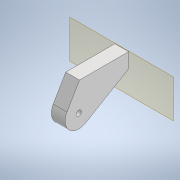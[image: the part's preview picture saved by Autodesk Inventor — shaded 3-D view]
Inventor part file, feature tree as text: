
AUTODESK INVENTOR PART (.ipt)
format: ipt  version: 2022 (Build 260153000, 153)  size: 130,048 bytes
history: native  units: in
note: dims shown in document units (in); Inventor stores cm internally (conversion verified against a paired STEP export)
features: reference x5, other x3, extrude x2, sketch x2, plane x1
ambient origin geometry x8: Origin, YZ Plane, XZ Plane, XY Plane, X Axis, Y Axis, Z Axis, Center Point
bodies: Solid1 (feature_tree)
feature tree (13):
  plane  "Work Plane1"
  extrude  "Extrusion1"  Depth=0.0079in
  extrude  "Extrusion2"  Depth=0.4724in
  sketch  "Sketch1"  dims[d0=0.0079in d1=0.0079in]
  reference  "Reference1"
  reference  "Reference4"
  reference  "Reference5"
  reference  "Reference6"
  sketch  "Sketch2"  dims[d3=0.1575in d4=0.1575in d5=1.5748in d6=0.0in d7=0.1693in d8=1.5748in d9=0.0in d10=0.1575in d11=0.1181in d12=0.1181in d14=0.4724in]
  reference  "Reference7"
  other  "Linear Rail Assembly.iam"
  other  "pivot module base:1"
  other  "cantilever:1"
